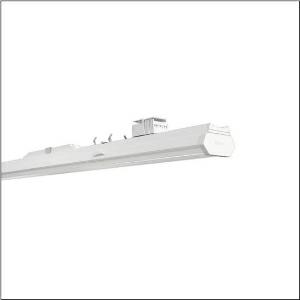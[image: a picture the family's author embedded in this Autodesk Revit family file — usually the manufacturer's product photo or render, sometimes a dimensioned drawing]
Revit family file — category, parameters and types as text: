
# Revit family: licross_r__11_protected_mo_51tp12dn49xf3s_c92a
name_source: partatom
category: Lighting Fixtures
units: mm (PartAtom-declared; Revit-internal decimal feet)

## family parameters
Cut with Voids When Loaded = No
Host = Face
Light Source = No
Part Type = Normal
Room Calculation Point = No
Round Connector Dimension = Use Diameter
Shared = No

## types (1)
- --- (1 x LED, 870 lm, 5 W, 4000K)
    Apparent Load = 5 VA
    CIE Flux Codes = 73 92 98 99 100
    Color Rendering = 80
    Color Temperature = 4000K
    Default Elevation = 1800 mm
    Description = Licross® 11 Protected MO, luminaire insert, of sheet steel, galvanised, coil coated, white, length: 1.500mm, width: 90mm, height: 101mm, LED rated luminous flux: 9.020lm, light colour: 840, control gear: DALI 2, control gear: ECG DALI, with plug, 6-pole, with phase selection, for trunking rail, 14-core, mains connection: 220..240V, AC/DC, 0/50..60Hz, halogen-free wiring, for emergency light function, converter,control gear: single battery element, battery: LiFeP04, 9Ah, primary optical cover: cover, of PMMA, light emission: direct with ceiling illumination distribution, protection rating (complete): IP64, insulation class (complete): insulation class I (protective earthing), certification: CE, UKCA, protection symbol: D if used in an environment with conductive dust loads with corresponding accessories, permissible ambient temperature for indoor applications: +5..+35°C, standard: EN 60598-2-22, corresponds to IFS (International Featured Standards) requirements for safety and quality in the food industry, reducing of maximum allowable ambient temperature of 5°C with ceiling mounting, LABS conformity tested according to VDMA 24364:2018-05, packaging unit: 1 piece
    Height = 92 mm
    Lamp = 1 x LED
    Lamp Light Flux = 870 lm
    Lamp Power = 5 W
    Lamp count = 1
    Length = 1500 mm
    Luminous efficacy = 174 lm/W
    Manufacturer = Siteco
    ModVariant = No
    Model = 51TP12DN49XF3S
    Mounting Place = Ceiling
    Mounting Type = Pendant
    Number of Poles = 1
    OnlyDefault = Yes
    Power Factor = 1
    Product Name = Licross® 11 Protected MO
    Product group = luminaire insert
    ProductGroupID = 902
    Protection Class = Protection class I
    Protection Degree = IP 64
    RLX_Detail_Level = 1
    RlxData = <blob elided: 24801 chars, md5=899c7543>
    Socket = socket
    Standby Power = 0 W
    System Light Flux = 870 lm
    System Power = 5 W
    Type Comments = : emergency light operation: 3 h
    Type Image = l_1256148.jpg
    URL = http://relux.com
    VarID = @adj_126035
    Voltage = 0 V
    Weight = 0.00 kg
    Width = 88 mm

## geometry (parser evidence)
native form markers: Blend x4, Sweep x10
no freeform markers — native parametric forms only
